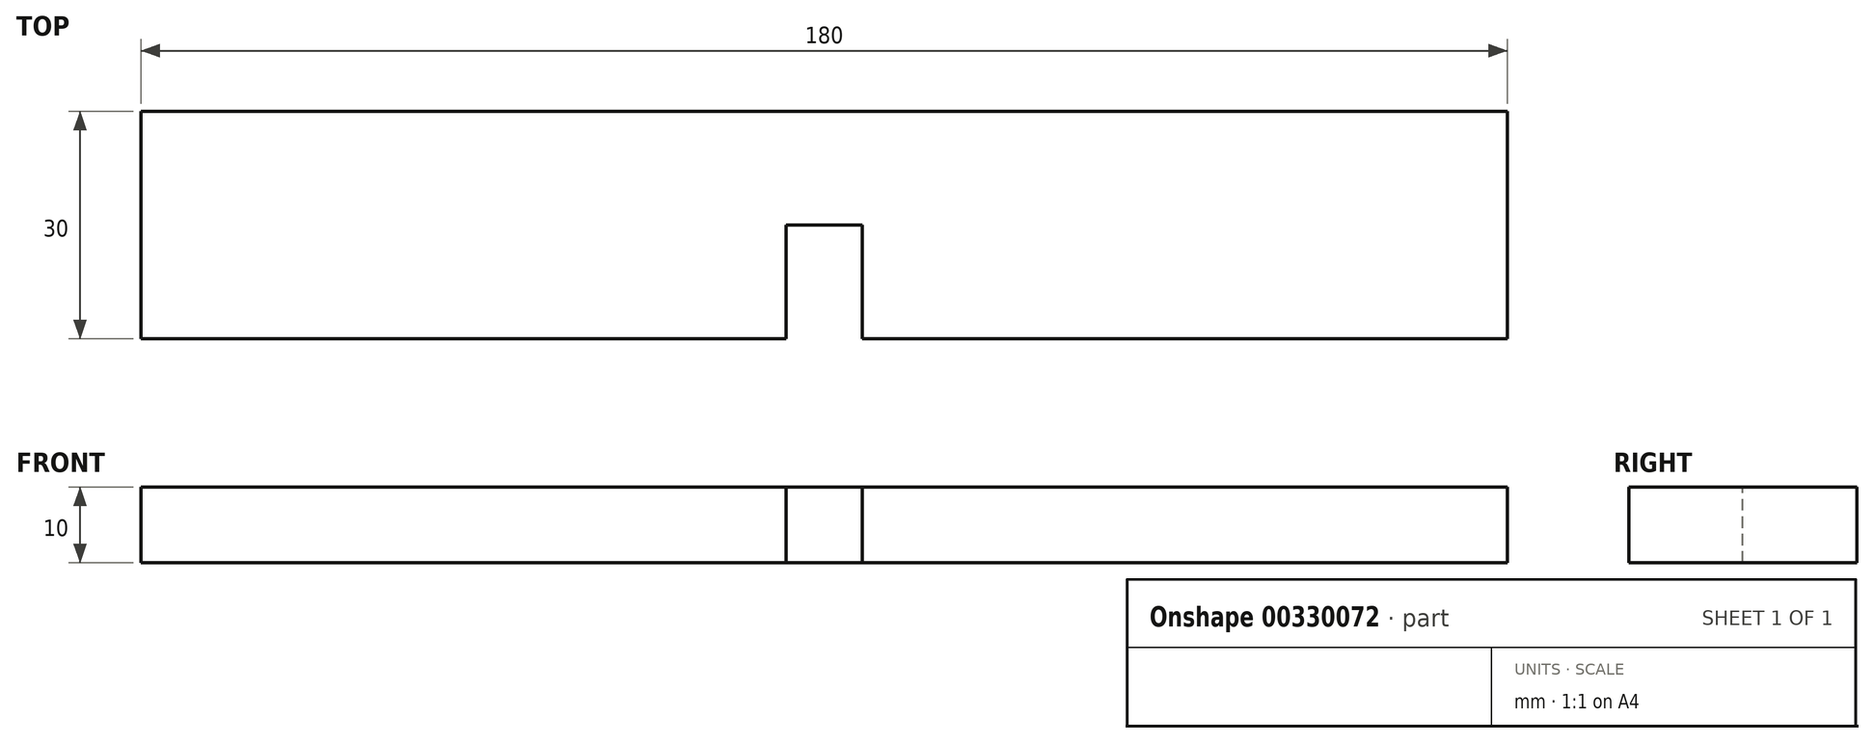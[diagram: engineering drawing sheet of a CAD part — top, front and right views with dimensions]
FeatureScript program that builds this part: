
annotation { "Feature Type Name" : "Feature", "Feature Type Description" : "" }
export const myFeature = defineFeature(function(context is Context, id is Id, definition is map)
    precondition{}
    {
        {
            var Q0;
            Q0=qCreatedBy(makeId("Front.planeOp"),FACE);
            var sketch = newSketch(context, id + "F0", { "sketchPlane" : qUnion([Q0])});
            skLineSegment(sketch, "E0.bottom", {"start": v(-233.22, 27.03) * mm, "end": v(-53.22, 27.03) * mm});
            skLineSegment(sketch, "E0.top", {"start": v(-233.22, 17.03) * mm, "end": v(-53.22, 17.03) * mm});
            skLineSegment(sketch, "E0.left", {"start": v(-233.22, 27.03) * mm, "end": v(-233.22, 17.03) * mm});
            skLineSegment(sketch, "E0.right", {"start": v(-53.22, 27.03) * mm, "end": v(-53.22, 17.03) * mm});
            skSolve(sketch);
        }
        {
            var Q0;
            Q0 = qSketchRegion(id + "F0", true);
            extrude(context, id + "F1", {"entities" : qUnion([Q0]), "depth" : 30 * mm, "offsetDistance" : 25 * mm});
        }
        {
            var Q0;
            Q0=makeQuery(id+"F1.opExtrude","SWEPT_FACE",FACE,{"disambiguationData":[OSD([sQuery(id+"F0.wireOp",EDGE,"E0.bottom")])]});
            var sketch = newSketch(context, id + "F2", { "sketchPlane" : qUnion([Q0])});
            skLineSegment(sketch, "E1", {"start": v(-143.22, 0) * mm, "end": v(-143.22, -15) * mm});
            skLineSegment(sketch, "E2", {"start": v(-148.22, 0) * mm, "end": v(-148.22, -30) * mm});
            skLineSegment(sketch, "E3", {"start": v(-138.22, 0) * mm, "end": v(-138.22, -30) * mm});
            skLineSegment(sketch, "E4", {"start": v(-148.22, -15) * mm, "end": v(-138.22, -15) * mm});
            skSolve(sketch);
        }
        {
            var Q0;
            {var subQ4=sQuery(id+"F2.wireOp",EDGE,"E2");var subQ6=makeQuery(id+"F1.opExtrude","CAP_EDGE",EDGE,{"disambiguationData":[OSD([sQuery(id+"F0.wireOp",EDGE,"E0.bottom")])],"isStart":false});var subQ8=makeQuery(id+"F2.imprint","INTERSECT",VERTEX,{"derivedFrom":[subQ6,subQ4]});Q0=makeQuery(id+"F2.imprint","IMPRINT",FACE,{"disambiguationData":[TD([[makeQuery(id+"F2.imprint","IMPRINT",EDGE,{"disambiguationData":[TD([[subQ8,1.0]])],"derivedFrom":subQ4}),1.0]])]});}
            extrude(context, id + "F3", {"entities" : qUnion([Q0]), "operationType" : NewBodyOperationType.REMOVE, "oppositeDirection" : true, "depth" : 25 * mm, "offsetDistance" : 25 * mm});
        }
    });
